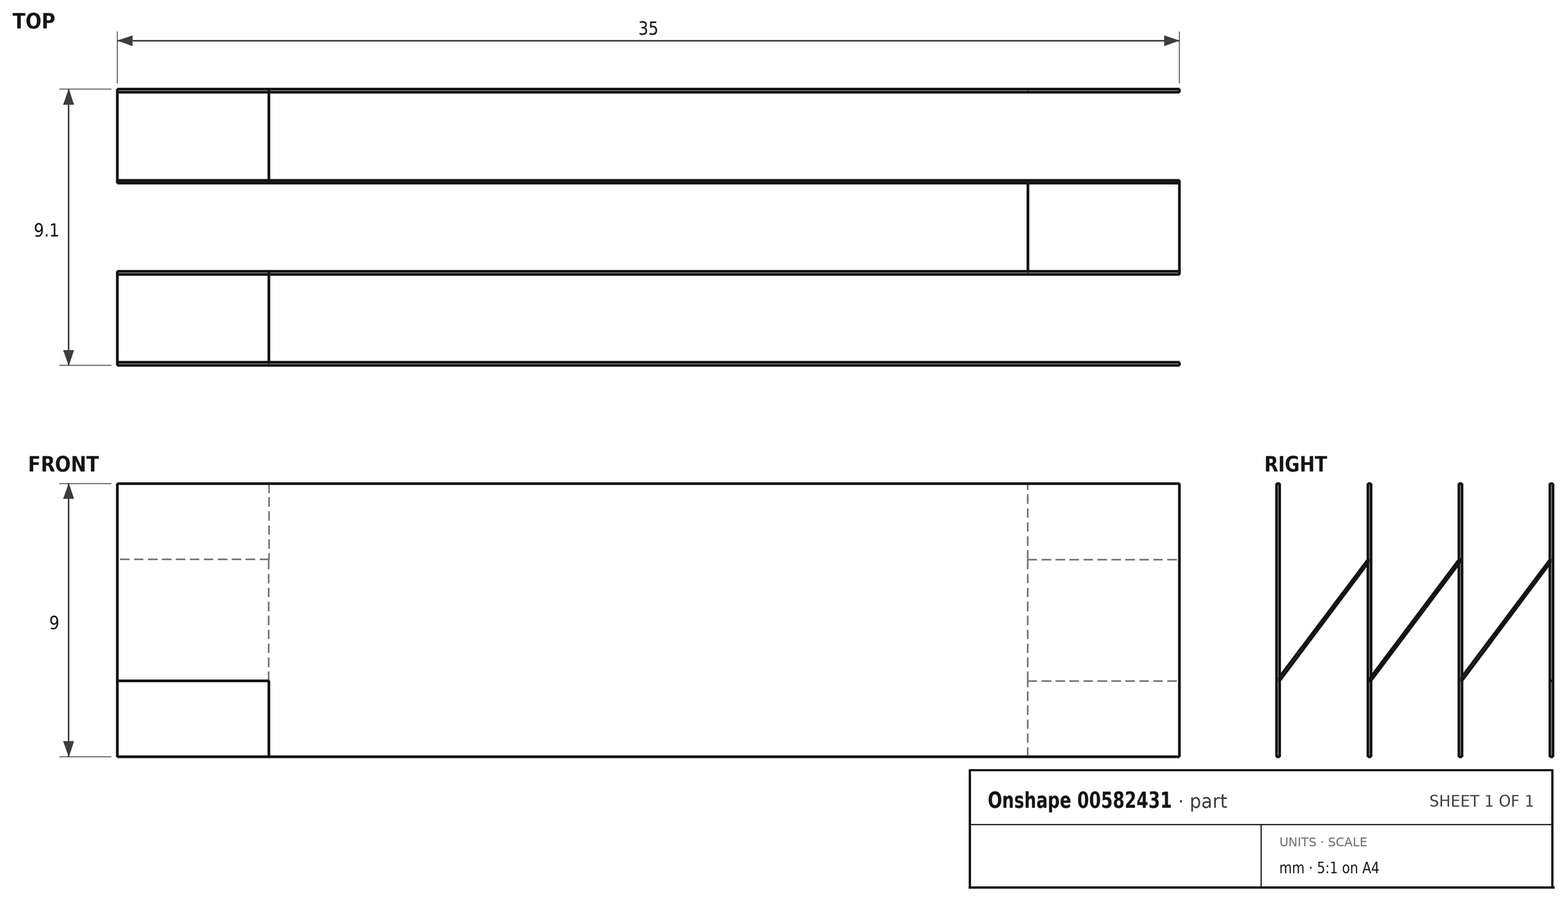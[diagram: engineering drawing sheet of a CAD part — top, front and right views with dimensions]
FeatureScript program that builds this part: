
annotation { "Feature Type Name" : "Feature", "Feature Type Description" : "" }
export const myFeature = defineFeature(function(context is Context, id is Id, definition is map)
    precondition{}
    {
        {
            var Q0;
            Q0=qCreatedBy(makeId("Front.planeOp"),FACE);
            var sketch = newSketch(context, id + "F0", { "sketchPlane" : qUnion([Q0])});
            skLineSegment(sketch, "E0", {"start": v(0, 0) * mm, "end": v(30, 0) * mm});
            skLineSegment(sketch, "E1", {"start": v(30, 0) * mm, "end": v(30, 9) * mm});
            skLineSegment(sketch, "E2", {"start": v(30, 9) * mm, "end": v(-5, 9) * mm});
            skLineSegment(sketch, "E3", {"start": v(-5, 9) * mm, "end": v(-5, 2.5) * mm});
            skLineSegment(sketch, "E4", {"start": v(-5, 2.5) * mm, "end": v(0, 2.5) * mm});
            skLineSegment(sketch, "E5", {"start": v(0, 2.5) * mm, "end": v(0, 0) * mm});
            skSolve(sketch);
        }
        {
            var Q0;
            Q0=qCreatedBy(makeId("Front.planeOp"),FACE);
            cPlane(context, id + "F1", {"entities" : qUnion([Q0]), "cplaneType" : CPlaneType.OFFSET, "offset" : 3 * mm, "oppositeDirection" : true, "width" : 150 * mm, "height" : 150 * mm});
        }
        {
            var Q0;
            Q0=qCreatedBy(id+"F1.planeOp",FACE);
            var sketch = newSketch(context, id + "F2", { "sketchPlane" : qUnion([Q0])});
            skLineSegment(sketch, "E6", {"start": v(0, 0) * mm, "end": v(-5, 0) * mm});
            skLineSegment(sketch, "E7", {"start": v(-5, 0) * mm, "end": v(-5, 6.5) * mm});
            skLineSegment(sketch, "E8", {"start": v(-5, 6.5) * mm, "end": v(0, 6.5) * mm});
            skLineSegment(sketch, "E9", {"start": v(0, 6.5) * mm, "end": v(0, 9) * mm});
            skLineSegment(sketch, "E10", {"start": v(0, 9) * mm, "end": v(30, 9) * mm});
            skLineSegment(sketch, "E11", {"start": v(30, 9) * mm, "end": v(30, 2.5) * mm});
            skLineSegment(sketch, "E12", {"start": v(30, 2.5) * mm, "end": v(25, 2.5) * mm});
            skLineSegment(sketch, "E13", {"start": v(25, 2.5) * mm, "end": v(25, 0) * mm});
            skLineSegment(sketch, "E14", {"start": v(25, 0) * mm, "end": v(0, 0) * mm});
            skSolve(sketch);
        }
        {
            var Q0;
            Q0=qCreatedBy(id+"F1.planeOp",FACE);
            cPlane(context, id + "F3", {"entities" : qUnion([Q0]), "cplaneType" : CPlaneType.OFFSET, "offset" : 3 * mm, "oppositeDirection" : true, "width" : 150 * mm, "height" : 150 * mm});
        }
        {
            var Q0;
            Q0=qCreatedBy(id+"F3.planeOp",FACE);
            var sketch = newSketch(context, id + "F4", { "sketchPlane" : qUnion([Q0])});
            skLineSegment(sketch, "E15", {"start": v(0, 0) * mm, "end": v(30, 0) * mm});
            skLineSegment(sketch, "E16", {"start": v(30, 0) * mm, "end": v(30, 6.5) * mm});
            skLineSegment(sketch, "E17", {"start": v(30, 6.5) * mm, "end": v(25, 6.5) * mm});
            skLineSegment(sketch, "E18", {"start": v(25, 6.5) * mm, "end": v(25, 9) * mm});
            skLineSegment(sketch, "E19", {"start": v(25, 9) * mm, "end": v(-5, 9) * mm});
            skLineSegment(sketch, "E20", {"start": v(-5, 9) * mm, "end": v(-5, 2.5) * mm});
            skLineSegment(sketch, "E21", {"start": v(-5, 2.5) * mm, "end": v(0, 2.5) * mm});
            skLineSegment(sketch, "E22", {"start": v(0, 2.5) * mm, "end": v(0, 0) * mm});
            skSolve(sketch);
        }
        {
            var Q0;
            Q0 = qBodyType(qCreatedBy(id + "F1CWV8CbvroxVGL_0" ,EDGE), BodyType.WIRE);
            var Q1;
            Q1=qCreatedBy(id+"F3.planeOp",FACE);
            cPlane(context, id + "F5", {"entities" : qUnion([Q0, Q1]), "cplaneType" : CPlaneType.OFFSET, "offset" : 3 * mm, "oppositeDirection" : true, "width" : 150 * mm, "height" : 150 * mm});
        }
        {
            var Q0;
            Q0=qCreatedBy(id+"F5.planeOp",FACE);
            var sketch = newSketch(context, id + "F6", { "sketchPlane" : qUnion([Q0])});
            skLineSegment(sketch, "E23", {"start": v(30, 9) * mm, "end": v(0, 9) * mm});
            skLineSegment(sketch, "E24", {"start": v(0, 9) * mm, "end": v(0, 6.5) * mm});
            skLineSegment(sketch, "E25", {"start": v(0, 6.5) * mm, "end": v(-5, 6.5) * mm});
            skLineSegment(sketch, "E26", {"start": v(-5, 6.5) * mm, "end": v(-5, 0) * mm});
            skLineSegment(sketch, "E27", {"start": v(-5, 0) * mm, "end": v(25, 0) * mm});
            skLineSegment(sketch, "E28", {"start": v(25, 0) * mm, "end": v(25, 2.5) * mm});
            skLineSegment(sketch, "E29", {"start": v(25, 2.5) * mm, "end": v(30, 2.5) * mm});
            skLineSegment(sketch, "E30", {"start": v(30, 2.5) * mm, "end": v(30, 9) * mm});
            skSolve(sketch);
        }
        {
            var Q0;
            Q0=sQuery(id+"F4.wireOp",EDGE,"E17");
            var Q1;
            Q1=sQuery(id+"F2.wireOp",EDGE,"E12");
            cPlane(context, id + "F7", {"entities" : qUnion([Q0, Q1]), "cplaneType" : CPlaneType.LINE_ANGLE, "offset" : 25 * mm, "angle" : 0 * degree, "width" : 150 * mm, "height" : 150 * mm});
        }
        {
            var Q0;
            Q0=qCreatedBy(id+"F7.planeOp",FACE);
            var sketch = newSketch(context, id + "F8", { "sketchPlane" : qUnion([Q0])});
            skLineSegment(sketch, "E31", {"start": v(30, 8.8) * mm, "end": v(30, 3.8) * mm});
            skLineSegment(sketch, "E32", {"start": v(30, 3.8) * mm, "end": v(25, 3.8) * mm});
            skLineSegment(sketch, "E33", {"start": v(25, 3.8) * mm, "end": v(25, 8.8) * mm});
            skLineSegment(sketch, "E34", {"start": v(25, 8.8) * mm, "end": v(30, 8.8) * mm});
            skSolve(sketch);
        }
        {
            var Q0;
            Q0=sQuery(id+"F2.wireOp",EDGE,"E8");
            var Q1;
            Q1=sQuery(id+"F0.wireOp",EDGE,"E4");
            cPlane(context, id + "F9", {"entities" : qUnion([Q0, Q1]), "cplaneType" : CPlaneType.LINE_ANGLE, "offset" : 25 * mm, "angle" : 0 * degree, "width" : 150 * mm, "height" : 150 * mm});
        }
        {
            var Q0;
            Q0=qCreatedBy(id+"F9.planeOp",FACE);
            var sketch = newSketch(context, id + "F10", { "sketchPlane" : qUnion([Q0])});
            skLineSegment(sketch, "E35", {"start": v(5, 7) * mm, "end": v(5, 2) * mm});
            skLineSegment(sketch, "E36", {"start": v(5, 2) * mm, "end": v(0, 2) * mm});
            skLineSegment(sketch, "E37", {"start": v(0, 2) * mm, "end": v(0, 7) * mm});
            skLineSegment(sketch, "E38", {"start": v(0, 7) * mm, "end": v(5, 7) * mm});
            skSolve(sketch);
        }
        {
            var Q0;
            Q0=sQuery(id+"F6.wireOp",EDGE,"E25");
            var Q1;
            Q1=sQuery(id+"F4.wireOp",EDGE,"E21");
            cPlane(context, id + "F11", {"entities" : qUnion([Q0, Q1]), "cplaneType" : CPlaneType.LINE_ANGLE, "offset" : 25 * mm, "angle" : 0 * degree, "width" : 150 * mm, "height" : 150 * mm});
        }
        {
            var Q0;
            Q0=qCreatedBy(id+"F11.planeOp",FACE);
            var sketch = newSketch(context, id + "F12", { "sketchPlane" : qUnion([Q0])});
            skLineSegment(sketch, "E39", {"start": v(-5, 10.6) * mm, "end": v(-5, 5.6) * mm});
            skLineSegment(sketch, "E40", {"start": v(-5, 5.6) * mm, "end": v(0, 5.6) * mm});
            skLineSegment(sketch, "E41", {"start": v(0, 5.6) * mm, "end": v(0, 10.6) * mm});
            skLineSegment(sketch, "E42", {"start": v(0, 10.6) * mm, "end": v(-5, 10.6) * mm});
            skSolve(sketch);
        }
        {
            var Q0;
            Q0 = qSketchRegion(id + "F2", true);
            var Q1;
            Q1 = qSketchRegion(id + "F0", true);
            var Q2;
            Q2 = qSketchRegion(id + "F4", true);
            var Q3;
            Q3 = qSketchRegion(id + "F6", true);
            var Q4;
            Q4 = qSketchRegion(id + "F8", true);
            var Q5;
            Q5 = qSketchRegion(id + "F10", true);
            var Q6;
            Q6 = qSketchRegion(id + "F12", true);
            extrude(context, id + "F13", {"entities" : qUnion([Q0, Q1, Q2, Q3, Q4, Q5, Q6]), "depth" : 0.1 * mm, "offsetDistance" : 25 * mm});
        }
    });
